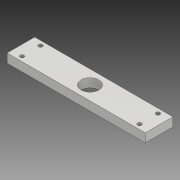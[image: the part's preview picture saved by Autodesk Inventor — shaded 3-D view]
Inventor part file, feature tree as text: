
AUTODESK INVENTOR PART (.ipt)
format: ipt  version: 2020 (Build 240168000, 168)  size: 109,056 bytes
history: native  units: mm
features: extrude x1, sketch x1
ambient origin geometry x8: Origin, YZ Plane, XZ Plane, XY Plane, X Axis, Y Axis, Z Axis, Center Point
bodies: Solid1 (feature_tree)
feature tree (2):
  extrude  "Extrusion1"  Depth=19.05mm
  sketch  "Sketch1"  dims[d0=300.0mm d1=150.0mm d2=38.5mm d3=60.0mm d4=30.0mm d5=8.5mm d6=22.5mm d7=22.5mm d8=22.5mm d9=22.5mm d10=10.0mm d11=10.0mm d12=10.0mm d13=10.0mm d14=19.05mm d15=0.0mm]
